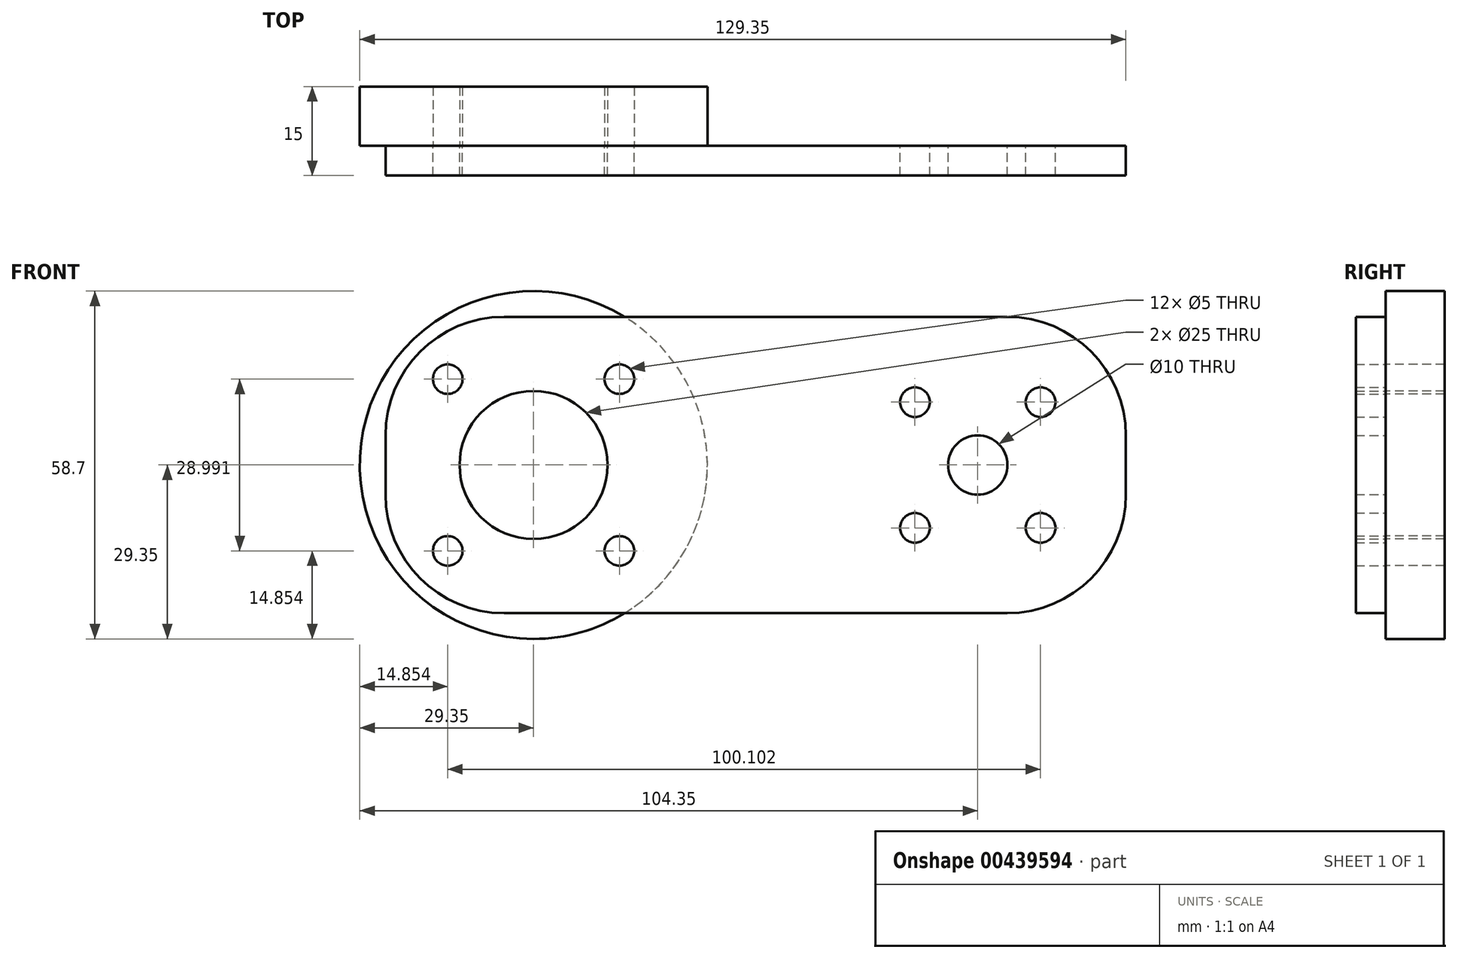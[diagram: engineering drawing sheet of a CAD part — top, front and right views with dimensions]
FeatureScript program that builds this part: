
annotation { "Feature Type Name" : "Feature", "Feature Type Description" : "" }
export const myFeature = defineFeature(function(context is Context, id is Id, definition is map)
    precondition{}
    {
        {
            var Q0;
            Q0=qCreatedBy(makeId("Front.planeOp"),FACE);
            var sketch = newSketch(context, id + "F0", { "sketchPlane" : qUnion([Q0])});
            skCircle(sketch, "E0", {"center": v(26.9, 10.6) * mm, "radius": 2.5 * mm});
            skCircle(sketch, "E1", {"center": v(26.9, -10.6) * mm, "radius": 2.5 * mm});
            skCircle(sketch, "E2", {"center": v(48.1, 10.6) * mm, "radius": 2.5 * mm});
            skCircle(sketch, "E3", {"center": v(48.1, -10.6) * mm, "radius": 2.5 * mm});
            skCircle(sketch, "E4", {"center": v(37.5, 0) * mm, "radius": 5 * mm});
            skLineSegment(sketch, "E5", {"start": v(26.9, 10.6) * mm, "end": v(37.5, 0) * mm});
            skLineSegment(sketch, "E6", {"start": v(48.1, 10.6) * mm, "end": v(37.5, 0) * mm});
            skCircle(sketch, "E7", {"center": v(-52, 14.5) * mm, "radius": 2.5 * mm});
            skCircle(sketch, "E8", {"center": v(-52, -14.5) * mm, "radius": 2.5 * mm});
            skCircle(sketch, "E9", {"center": v(-23, 14.5) * mm, "radius": 2.5 * mm});
            skCircle(sketch, "E10", {"center": v(-23, -14.5) * mm, "radius": 2.5 * mm});
            skCircle(sketch, "E11", {"center": v(-37.5, 0) * mm, "radius": 12.5 * mm});
            skLineSegment(sketch, "E12", {"start": v(-52, 14.5) * mm, "end": v(-37.5, 0) * mm});
            skLineSegment(sketch, "E13", {"start": v(-23, 14.5) * mm, "end": v(-37.5, 0) * mm});
            skLineSegment(sketch, "E14.bottom", {"start": v(42.5, 25) * mm, "end": v(-42.5, 25) * mm});
            skLineSegment(sketch, "E14.top", {"start": v(42.5, -25) * mm, "end": v(-42.5, -25) * mm});
            skLineSegment(sketch, "E14.left", {"start": v(62.5, 5) * mm, "end": v(62.5, -5) * mm});
            skLineSegment(sketch, "E14.right", {"start": v(-62.5, 5) * mm, "end": v(-62.5, -5) * mm});
            skPoint(sketch, "E14.middle", {"position": v(0, 0) * mm});
            skPoint(sketch, "E15.visualSharp", {"position": v(62.5, 25) * mm});
            skArc(sketch, "E15.filletArc", {"start": v(62.5, 5) * mm, "mid": v(56.64, 19.14) * mm, "end": v(42.5, 25) * mm});
            skPoint(sketch, "E16.visualSharp", {"position": v(62.5, -25) * mm});
            skArc(sketch, "E16.filletArc", {"start": v(42.5, -25) * mm, "mid": v(56.64, -19.14) * mm, "end": v(62.5, -5) * mm});
            skPoint(sketch, "E17.visualSharp", {"position": v(-62.5, 25) * mm});
            skArc(sketch, "E17.filletArc", {"start": v(-42.5, 25) * mm, "mid": v(-56.64, 19.14) * mm, "end": v(-62.5, 5) * mm});
            skPoint(sketch, "E18.visualSharp", {"position": v(-62.5, -25) * mm});
            skArc(sketch, "E18.filletArc", {"start": v(-62.5, -5) * mm, "mid": v(-56.64, -19.14) * mm, "end": v(-42.5, -25) * mm});
            skSolve(sketch);
        }
        {
            var Q0;
            Q0=makeQuery(id+"F0.imprint","IMPRINT",FACE,{"disambiguationData":[TD([[makeQuery(id+"F0.imprint","IMPRINT",EDGE,{"derivedFrom":sQuery(id+"F0.wireOp",EDGE,"E0")}),-1.0]])]});
            extrude(context, id + "F1", {"entities" : qUnion([Q0]), "depth" : 5 * mm});
        }
        {
            var Q0;
            Q0=qCreatedBy(makeId("Front.planeOp"),FACE);
            var sketch = newSketch(context, id + "F2", { "sketchPlane" : qUnion([Q0])});
            skCircle(sketch, "E19", {"center": v(-37.5, 0) * mm, "radius": 29.35 * mm});
            skCircle(sketch, "E20", {"center": v(-52, 14.5) * mm, "radius": 2.5 * mm});
            skCircle(sketch, "E21", {"center": v(-52, -14.5) * mm, "radius": 2.5 * mm});
            skCircle(sketch, "E22", {"center": v(-23, 14.5) * mm, "radius": 2.5 * mm});
            skCircle(sketch, "E23", {"center": v(-23, -14.5) * mm, "radius": 2.5 * mm});
            skCircle(sketch, "E24", {"center": v(-37.5, 0) * mm, "radius": 12.5 * mm});
            skLineSegment(sketch, "E25", {"start": v(-52, 14.5) * mm, "end": v(-37.5, 0) * mm});
            skLineSegment(sketch, "E26", {"start": v(-37.5, 0) * mm, "end": v(-23, 14.5) * mm});
            skLineSegment(sketch, "E27", {"start": v(-37.5, 0) * mm, "end": v(-23, -14.5) * mm});
            skLineSegment(sketch, "E28", {"start": v(-37.5, 0) * mm, "end": v(-52, -14.5) * mm});
            skSolve(sketch);
        }
        {
            var Q0;
            Q0=qSketchRegion(id+"F2",true);
            extrude(context, id + "F3", {"entities" : qUnion([Q0]), "oppositeDirection" : true, "depth" : 10 * mm});
        }
    });
